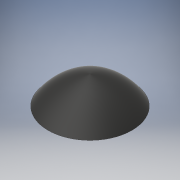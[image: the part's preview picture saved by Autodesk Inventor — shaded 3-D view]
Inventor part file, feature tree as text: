
AUTODESK INVENTOR PART (.ipt)
format: ipt  version: 2019 (Build 230136000, 136)  size: 116,224 bytes
history: native  units: mm
features: revolve x1, sketch x1
ambient origin geometry x8: Origin, YZ Plane, XZ Plane, XY Plane, X Axis, Y Axis, Z Axis, Center Point
bodies: Solid1 (feature_tree)
feature tree (2):
  revolve  "Revolution1"  [1 undecoded]
  sketch  "Sketch1"  dims[d0=3.0mm d1=2.0mm d2=90.0deg]
note: 1 required parameter value undecoded (feature->parameter linkage not recoverable at this tier; creation-order binding heuristic only, values carry confidence <= 0.55)
